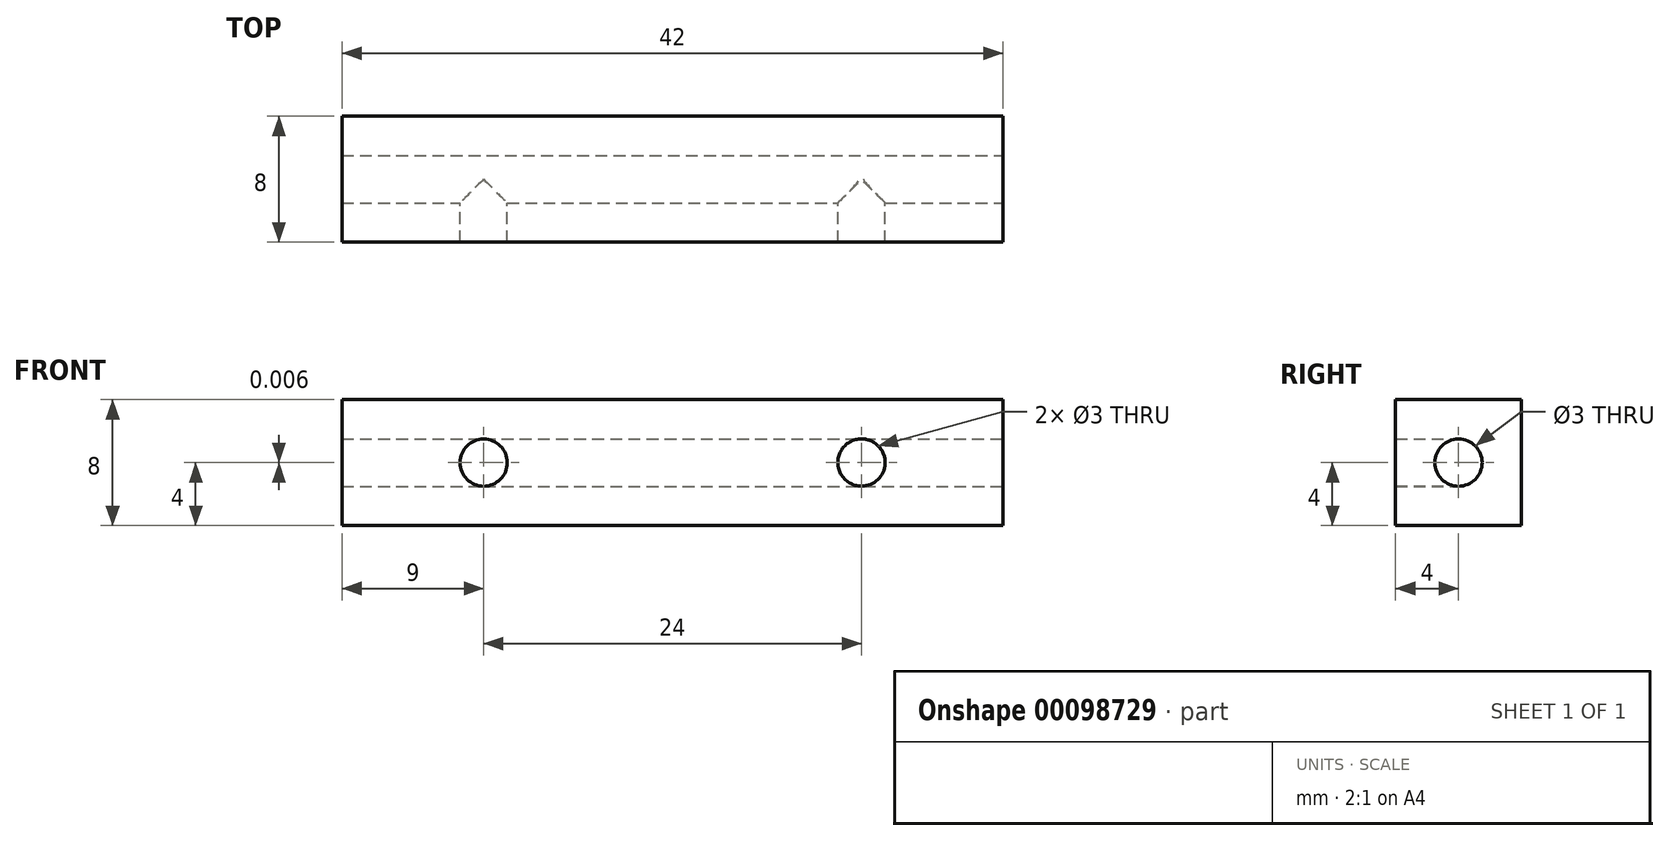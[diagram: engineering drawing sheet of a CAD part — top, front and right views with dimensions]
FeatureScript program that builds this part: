
annotation { "Feature Type Name" : "Feature", "Feature Type Description" : "" }
export const myFeature = defineFeature(function(context is Context, id is Id, definition is map)
    precondition{}
    {
        {
            var Q0;
            Q0=qCreatedBy(makeId("Front.planeOp"),FACE);
            var sketch = newSketch(context, id + "F0", { "sketchPlane" : qUnion([Q0])});
            skLineSegment(sketch, "E0.bottom", {"start": v(21, -4) * mm, "end": v(-21, -4) * mm});
            skLineSegment(sketch, "E0.top", {"start": v(21, 4) * mm, "end": v(-21, 4) * mm});
            skLineSegment(sketch, "E0.left", {"start": v(21, -4) * mm, "end": v(21, 4) * mm});
            skLineSegment(sketch, "E0.right", {"start": v(-21, -4) * mm, "end": v(-21, 4) * mm});
            skPoint(sketch, "E0.middle", {"position": v(0, 0) * mm});
            skCircle(sketch, "E1", {"center": v(-12, 0) * mm, "radius": 1.5 * mm});
            skCircle(sketch, "E2", {"center": v(12, 0) * mm, "radius": 1.5 * mm});
            skSolve(sketch);
        }
        {
            var Q0;
            Q0=makeQuery(id+"F0.imprint","IMPRINT",FACE,{"disambiguationData":[TD([[makeQuery(id+"F0.imprint","IMPRINT",EDGE,{"derivedFrom":sQuery(id+"F0.wireOp",EDGE,"E0.bottom")}),-1.0]])]});
            extrude(context, id + "F1", {"entities" : qUnion([Q0]), "depth" : 8 * mm});
        }
        {
            var Q0;
            Q0=makeQuery(id+"F0.imprint","IMPRINT",FACE,{"disambiguationData":[TD([[makeQuery(id+"F0.imprint","IMPRINT",EDGE,{"derivedFrom":sQuery(id+"F0.wireOp",EDGE,"E1")}),1.0]])]});
            var Q1;
            Q1=makeQuery(id+"F0.imprint","IMPRINT",FACE,{"disambiguationData":[TD([[makeQuery(id+"F0.imprint","IMPRINT",EDGE,{"derivedFrom":sQuery(id+"F0.wireOp",EDGE,"E2")}),1.0]])]});
            extrude(context, id + "F2", {"entities" : qUnion([Q0, Q1]), "operationType" : NewBodyOperationType.ADD, "depth" : 4 * mm});
        }
        {
            var Q0;
            Q0=makeQuery(id+"F1.opExtrude","SWEPT_FACE",FACE,{"disambiguationData":[OSD([sQuery(id+"F0.wireOp",EDGE,"E0.left")])]});
            var sketch = newSketch(context, id + "F3", { "sketchPlane" : qUnion([Q0])});
            skCircle(sketch, "E3", {"center": v(-4, 0) * mm, "radius": 1.5 * mm});
            skSolve(sketch);
        }
        {
            var Q0;
            Q0=sQuery(id+"F3.wireOp",VERTEX,"E3.center");
            var Q1;
            Q1=makeQuery(id+"F1.opExtrude","SWEPT_BODY",BODY,{"disambiguationData":[OSD([sQuery(id+"F0.wireOp",EDGE,"E0.bottom"),sQuery(id+"F0.wireOp",EDGE,"E0.top"),sQuery(id+"F0.wireOp",EDGE,"E0.left"),sQuery(id+"F0.wireOp",EDGE,"E0.right"),sQuery(id+"F0.wireOp",EDGE,"E1"),sQuery(id+"F0.wireOp",EDGE,"E2")])]});
            hole(context, id + "F4", {"style" : HoleStyle.SIMPLE, "endStyle" : HoleEndStyle.THROUGH, "holeDiameter" : 3 * mm, "locations" : qUnion([Q0]), "scope" : qUnion([Q1]), "isTappedThrough" : true});
        }
    });
